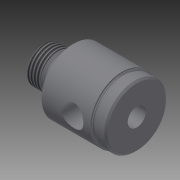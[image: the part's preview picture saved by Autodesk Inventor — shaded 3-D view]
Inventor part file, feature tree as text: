
AUTODESK INVENTOR PART (.ipt)
format: ipt  version: 2014 (Build 180170000, 170)  size: 257,024 bytes
history: native  units: in
note: dims shown in document units (in); Inventor stores cm internally (conversion verified against a paired STEP export)
features: other x112, sketch x5, revolve x4, thread x1, hole x1
ambient origin geometry x8: Origin, YZ Plane, XZ Plane, XY Plane, X Axis, Y Axis, Z Axis, Center Point
bodies: Solid1 (feature_tree)
feature tree (123):
  revolve  "Revolution1"  [1 undecoded]
  thread  "Thread1"  [1 undecoded]
  revolve  "Revolution2"  Angle=360.0deg
  hole  "Hole1"  [1 undecoded]
  revolve  "Revolution3"  [1 undecoded]
  revolve  "Revolution4"  [1 undecoded]
  other  "dp1_XY"
  other  "dp1_YZ"
  other  "dp1_ZX"
  other  "dp1_X"
  other  "dp1_Y"
  other  "dp1_Z"
  other  "dp1_Center"
  other  "dp2_XY"
  other  "dp2_YZ"
  other  "dp2_ZX"
  other  "dp2_X"
  other  "dp2_Y"
  other  "dp2_Z"
  other  "dp2_Center"
  other  "port_XY"
  other  "port_YZ"
  other  "port_ZX"
  other  "port_X"
  other  "port_Y"
  other  "port_Z"
  other  "port_Center"
  other  "rod_guide_XY"
  other  "rod_guide_YZ"
  other  "rod_guide_ZX"
  other  "rod_guide_X"
  other  "rod_guide_Y"
  other  "rod_guide_Z"
  other  "rod_guide_Center"
  other  "s1_XY"
  other  "s1_YZ"
  other  "s1_ZX"
  other  "s1_X"
  other  "s1_Y"
  other  "s1_Z"
  other  "s1_Center"
  other  "s2_XY"
  other  "s2_YZ"
  other  "s2_ZX"
  other  "s2_X"
  other  "s2_Y"
  other  "s2_Z"
  other  "s2_Center"
  other  "t1_XY"
  other  "t1_YZ"
  other  "t1_ZX"
  other  "t1_X"
  other  "t1_Y"
  other  "t1_Z"
  other  "t1_Center"
  other  "t111_XY"
  other  "t111_YZ"
  other  "t111_ZX"
  other  "t111_X"
  other  "t111_Y"
  other  "t111_Z"
  other  "t111_Center"
  other  "to_foot_bracket_XY"
  other  "to_foot_bracket_YZ"
  other  "to_foot_bracket_ZX"
  other  "to_foot_bracket_X"
  other  "to_foot_bracket_Y"
  other  "to_foot_bracket_Z"
  other  "to_foot_bracket_Center"
  other  "to_nut_XY"
  other  "to_nut_YZ"
  other  "to_nut_ZX"
  other  "to_nut_X"
  other  "to_nut_Y"
  other  "to_nut_Z"
  other  "to_nut_Center"
  other  "to_rod_XY"
  other  "to_rod_YZ"
  other  "to_rod_ZX"
  other  "to_rod_X"
  other  "to_rod_Y"
  other  "to_rod_Z"
  other  "to_rod_Center"
  other  "to_screw_XY"
  other  "to_screw_YZ"
  other  "to_screw_ZX"
  other  "to_screw_X"
  other  "to_screw_Y"
  other  "to_screw_Z"
  other  "to_screw_Center"
  other  "to_trunnion_brackets_XY"
  other  "to_trunnion_brackets_YZ"
  other  "to_trunnion_brackets_ZX"
  other  "to_trunnion_brackets_X"
  other  "to_trunnion_brackets_Y"
  other  "to_trunnion_brackets_Z"
  other  "to_trunnion_brackets_Center"
  other  "to_trunnion_brackets1_XY"
  other  "to_trunnion_brackets1_YZ"
  other  "to_trunnion_brackets1_ZX"
  other  "to_trunnion_brackets1_X"
  other  "to_trunnion_brackets1_Y"
  other  "to_trunnion_brackets1_Z"
  other  "to_trunnion_brackets1_Center"
  other  "to_trunnion_brackets2_XY"
  other  "to_trunnion_brackets2_YZ"
  other  "to_trunnion_brackets2_ZX"
  other  "to_trunnion_brackets2_X"
  other  "to_trunnion_brackets2_Y"
  other  "to_trunnion_brackets2_Z"
  other  "to_trunnion_brackets2_Center"
  other  "to_tube_XY"
  other  "to_tube_YZ"
  other  "to_tube_ZX"
  other  "to_tube_X"
  other  "to_tube_Y"
  other  "to_tube_Z"
  other  "to_tube_Center"
  sketch  "Sketch_2"  dims[d0=360.0deg d1=0.2297in d2=0.0in d3=360.0deg]
  sketch  "Sketch_3"  dims[d4=0.316in d5=0.75in d6=0.376in d7=0.25in d8=90.0deg d9=1.625in d10=0.0in d11=360.0deg]
  sketch  "Sketch3"  dims[d12=360.0deg]
  sketch  "Sketch_40"
  sketch  "Sketch_47"
note: 5 required parameter values undecoded (feature->parameter linkage not recoverable at this tier; creation-order binding heuristic only, values carry confidence <= 0.55)